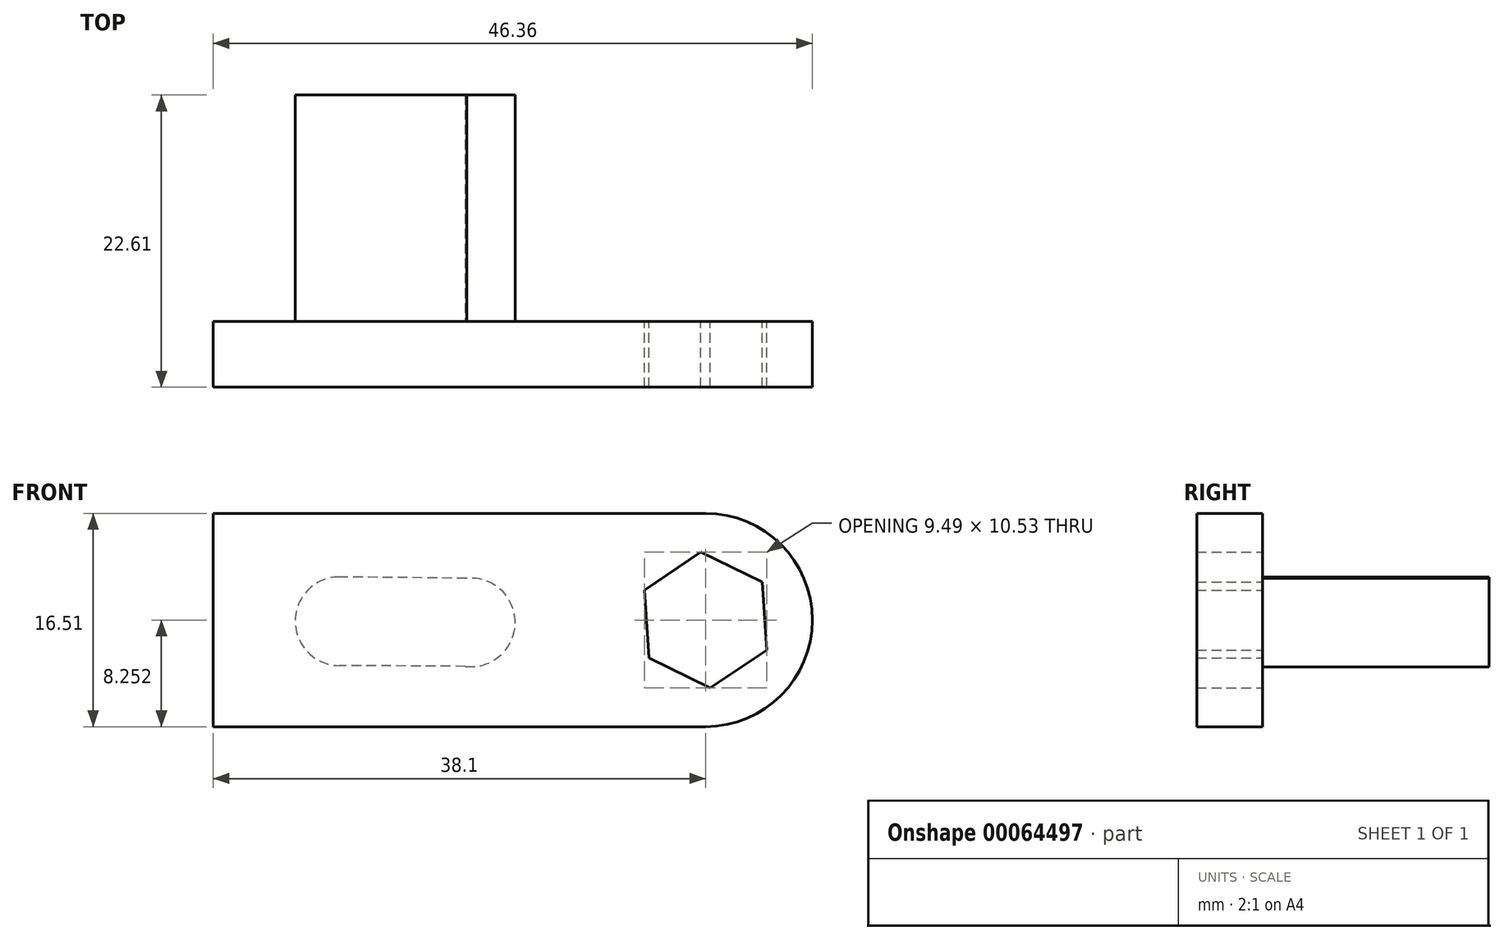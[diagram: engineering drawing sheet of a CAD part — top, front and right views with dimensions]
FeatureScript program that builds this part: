
annotation { "Feature Type Name" : "Feature", "Feature Type Description" : "" }
export const myFeature = defineFeature(function(context is Context, id is Id, definition is map)
    precondition{}
    {
        {
            var Q0;
            Q0=qCreatedBy(makeId("Front.planeOp"),FACE);
            var sketch = newSketch(context, id + "F0", { "sketchPlane" : qUnion([Q0])});
            skLineSegment(sketch, "E0", {"start": v(-75.02, 12.05) * mm, "end": v(-75.02, -4.46) * mm});
            skLineSegment(sketch, "E1", {"start": v(-75.02, -4.46) * mm, "end": v(-36.92, -4.46) * mm});
            skLineSegment(sketch, "E2", {"start": v(-75.02, 12.05) * mm, "end": v(-36.92, 12.05) * mm});
            skArc(sketch, "E3", {"start": v(-36.92, -4.46) * mm, "mid": v(-28.66, 3.8) * mm, "end": v(-36.92, 12.05) * mm});
            skCircle(sketch, "E4.cCircle", {"center": v(-36.92, 3.8) * mm, "radius": 4.57 * mm, "construction": true});
            skLineSegment(sketch, "E4.0", {"start": v(-32.18, 1.47) * mm, "end": v(-36.56, -1.47) * mm});
            skLineSegment(sketch, "E4.1", {"start": v(-36.56, -1.47) * mm, "end": v(-41.3, 0.84) * mm});
            skLineSegment(sketch, "E4.2", {"start": v(-41.3, 0.84) * mm, "end": v(-41.66, 6.11) * mm});
            skLineSegment(sketch, "E4.3", {"start": v(-41.66, 6.11) * mm, "end": v(-37.28, 9.06) * mm});
            skLineSegment(sketch, "E4.4", {"start": v(-37.28, 9.06) * mm, "end": v(-32.54, 6.74) * mm});
            skLineSegment(sketch, "E4.5", {"start": v(-32.54, 6.74) * mm, "end": v(-32.18, 1.47) * mm});
            skPoint(sketch, "E4.0.midPoint", {"position": v(-34.37, 0) * mm});
            skSolve(sketch);
        }
        {
            var Q0;
            Q0=makeQuery(id+"F0.imprint","IMPRINT",FACE,{"disambiguationData":[TD([[makeQuery(id+"F0.imprint","IMPRINT",EDGE,{"derivedFrom":sQuery(id+"F0.wireOp",EDGE,"E0")}),1.0]])]});
            extrude(context, id + "F1", {"entities" : qUnion([Q0]), "depth" : 5.08 * mm});
        }
        {
            var Q0;
            Q0=makeQuery(id+"F1.opExtrude","CAP_FACE",FACE,{"disambiguationData":[OSD([sQuery(id+"F0.wireOp",EDGE,"E0"),sQuery(id+"F0.wireOp",EDGE,"E1"),sQuery(id+"F0.wireOp",EDGE,"E2"),sQuery(id+"F0.wireOp",EDGE,"E3"),sQuery(id+"F0.wireOp",EDGE,"E4.0"),sQuery(id+"F0.wireOp",EDGE,"E4.1"),sQuery(id+"F0.wireOp",EDGE,"E4.2"),sQuery(id+"F0.wireOp",EDGE,"E4.3"),sQuery(id+"F0.wireOp",EDGE,"E4.4"),sQuery(id+"F0.wireOp",EDGE,"E4.5")])],"isStart":true});
            var sketch = newSketch(context, id + "F2", { "sketchPlane" : qUnion([Q0])});
            skLineSegment(sketch, "E5", {"start": v(41.48, 3.48) * mm, "end": v(75.02, 3.8) * mm, "construction": true});
            skCircle(sketch, "E6", {"center": v(65.24, 3.7) * mm, "radius": 3.43 * mm});
            skCircle(sketch, "E7", {"center": v(55.08, 3.6) * mm, "radius": 3.43 * mm});
            skLineSegment(sketch, "E8", {"start": v(55.51, 0.2) * mm, "end": v(65.26, 0.27) * mm});
            skLineSegment(sketch, "E9", {"start": v(55.4, 7.02) * mm, "end": v(65.2, 7.13) * mm});
            skSolve(sketch);
        }
        {
            var Q0;
            {var subQ0=sQuery(id+"F2.wireOp",EDGE,"E8");Q0=makeQuery(id+"F2.imprint","IMPRINT",FACE,{"disambiguationData":[TD([[makeQuery(id+"F2.imprint","IMPRINT",EDGE,{"derivedFrom":subQ0}),1.0]])]});}
            var Q1;
            {var subQ0=sQuery(id+"F2.wireOp",EDGE,"E7");var subQ1=makeQuery(id+"F2.imprint","INTERSECT",VERTEX,{"derivedFrom":[subQ0,sQuery(id+"F2.wireOp",EDGE,"E8")]});Q1=makeQuery(id+"F2.imprint","IMPRINT",FACE,{"disambiguationData":[TD([[makeQuery(id+"F2.imprint","IMPRINT",EDGE,{"disambiguationData":[TD([[subQ1,1.0]])],"derivedFrom":subQ0}),1.0]])]});}
            var Q2;
            {var subQ0=sQuery(id+"F2.wireOp",EDGE,"E6");var subQ1=makeQuery(id+"F2.imprint","INTERSECT",VERTEX,{"derivedFrom":[subQ0,sQuery(id+"F2.wireOp",EDGE,"E8")]});Q2=makeQuery(id+"F2.imprint","IMPRINT",FACE,{"disambiguationData":[TD([[makeQuery(id+"F2.imprint","IMPRINT",EDGE,{"disambiguationData":[TD([[subQ1,1.0]])],"derivedFrom":subQ0}),1.0]])]});}
            extrude(context, id + "F3", {"entities" : qUnion([Q0, Q1, Q2]), "operationType" : NewBodyOperationType.ADD, "depth" : 17.53 * mm});
        }
    });
